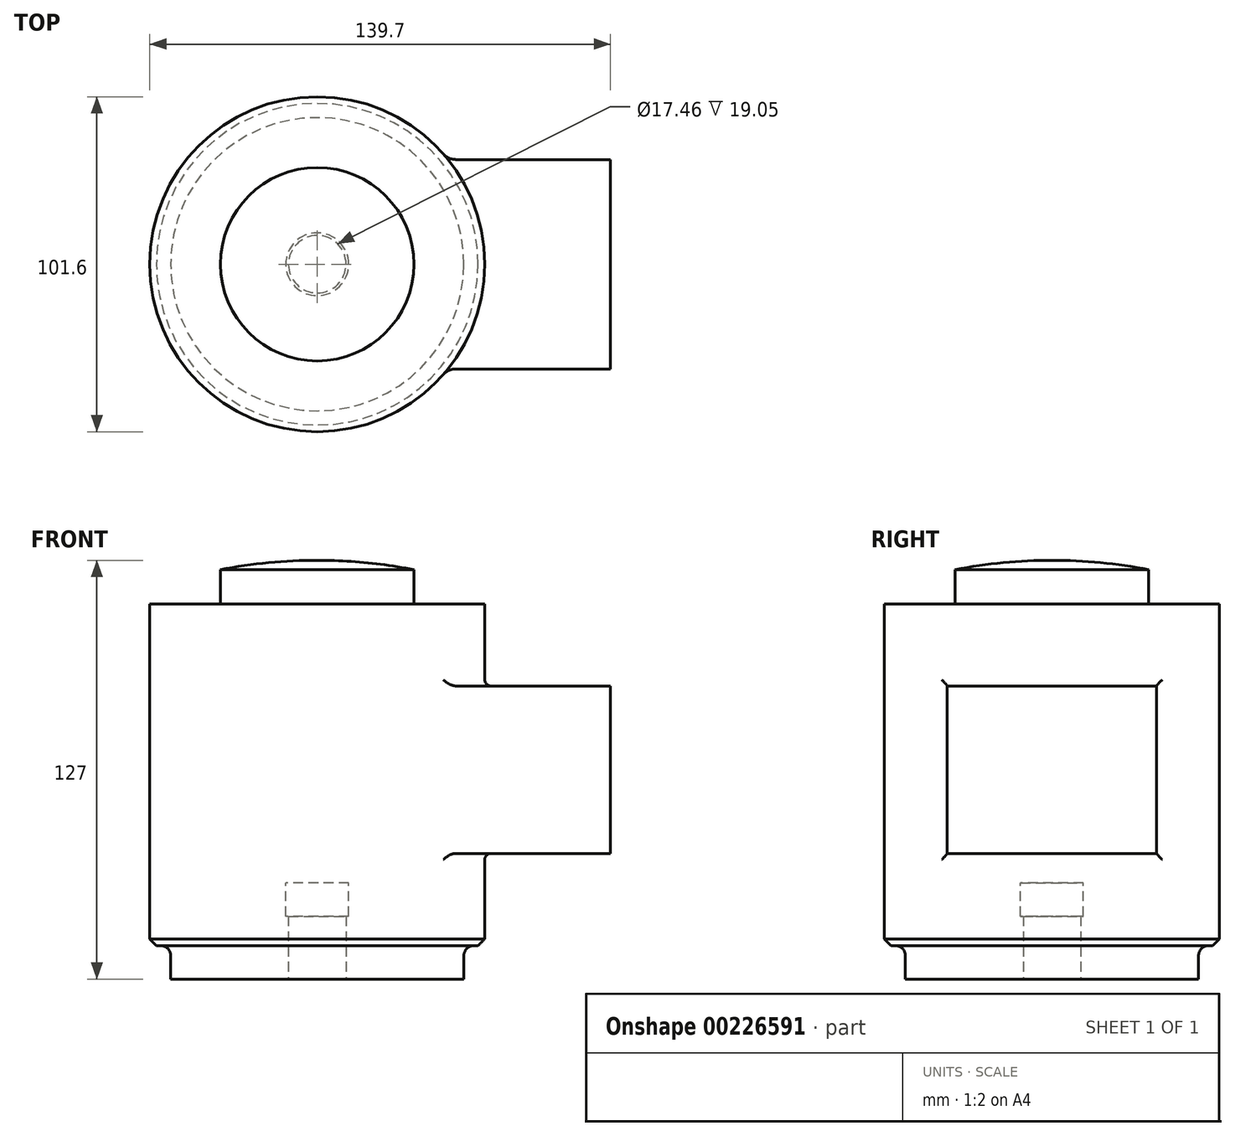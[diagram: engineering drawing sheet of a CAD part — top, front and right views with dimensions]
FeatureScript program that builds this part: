
annotation { "Feature Type Name" : "Feature", "Feature Type Description" : "" }
export const myFeature = defineFeature(function(context is Context, id is Id, definition is map)
    precondition{}
    {
        {
            var Q0;
            Q0=qCreatedBy(makeId("Front.planeOp"),FACE);
            var sketch = newSketch(context, id + "F0", { "sketchPlane" : qUnion([Q0])});
            skLineSegment(sketch, "E0.bottom", {"start": v(44.45, 0) * mm, "end": v(-44.45, 0) * mm});
            skLineSegment(sketch, "E0.top", {"start": v(44.45, 10.16) * mm, "end": v(-44.45, 10.16) * mm});
            skLineSegment(sketch, "E0.left", {"start": v(44.45, 0) * mm, "end": v(44.45, 10.16) * mm});
            skLineSegment(sketch, "E0.right", {"start": v(-44.45, 0) * mm, "end": v(-44.45, 10.16) * mm});
            skLineSegment(sketch, "E1.bottom", {"start": v(50.8, 10.16) * mm, "end": v(-50.8, 10.16) * mm});
            skLineSegment(sketch, "E1.top", {"start": v(50.8, 113.8) * mm, "end": v(-50.8, 113.8) * mm});
            skLineSegment(sketch, "E1.left", {"start": v(50.8, 10.16) * mm, "end": v(50.8, 113.8) * mm});
            skLineSegment(sketch, "E1.right", {"start": v(-50.8, 10.16) * mm, "end": v(-50.8, 113.8) * mm});
            skPoint(sketch, "E1.middle", {"position": v(0, 61.98) * mm});
            skLineSegment(sketch, "E2.bottom", {"start": v(29.34, 113.8) * mm, "end": v(-29.34, 113.8) * mm});
            skLineSegment(sketch, "E2.top", {"start": v(29.34, 124.15) * mm, "end": v(-29.34, 124.15) * mm});
            skLineSegment(sketch, "E2.left", {"start": v(29.34, 113.8) * mm, "end": v(29.34, 124.15) * mm});
            skLineSegment(sketch, "E2.right", {"start": v(-29.34, 113.8) * mm, "end": v(-29.34, 124.15) * mm});
            skPoint(sketch, "E2.middle", {"position": v(0, 118.97) * mm});
            skArc(sketch, "E3", {"start": v(29.34, 124.15) * mm, "mid": v(0, 127) * mm, "end": v(-29.34, 124.15) * mm});
            skLineSegment(sketch, "E4.bottom", {"start": v(0, 38.1) * mm, "end": v(88.9, 38.1) * mm});
            skLineSegment(sketch, "E4.top", {"start": v(0, 88.9) * mm, "end": v(88.9, 88.9) * mm});
            skLineSegment(sketch, "E4.left", {"start": v(0, 38.1) * mm, "end": v(0, 88.9) * mm});
            skLineSegment(sketch, "E4.right", {"start": v(88.9, 38.1) * mm, "end": v(88.9, 88.9) * mm});
            skLineSegment(sketch, "E5", {"start": v(0, 0) * mm, "end": v(0, 127) * mm});
            skLineSegment(sketch, "E6.bottom", {"start": v(9.53, 19.05) * mm, "end": v(-9.52, 19.05) * mm});
            skLineSegment(sketch, "E6.top", {"start": v(9.53, 29.21) * mm, "end": v(-9.52, 29.21) * mm});
            skLineSegment(sketch, "E6.left", {"start": v(9.53, 19.05) * mm, "end": v(9.53, 29.21) * mm});
            skLineSegment(sketch, "E6.right", {"start": v(-9.53, 19.05) * mm, "end": v(-9.52, 29.21) * mm});
            skPoint(sketch, "E6.middle", {"position": v(0, 24.13) * mm});
            skSolve(sketch);
        }
        {
            var Q0;
            {var subQ0=sQuery(id+"F0.wireOp",EDGE,"E0.right");Q0=makeQuery(id+"F0.imprint","IMPRINT",FACE,{"disambiguationData":[TD([[makeQuery(id+"F0.imprint","IMPRINT",EDGE,{"derivedFrom":subQ0}),-1.0]])]});}
            var Q1;
            {var subQ0=sQuery(id+"F0.wireOp",EDGE,"E1.right");Q1=makeQuery(id+"F0.imprint","IMPRINT",FACE,{"disambiguationData":[TD([[makeQuery(id+"F0.imprint","IMPRINT",EDGE,{"derivedFrom":subQ0}),-1.0]])]});}
            var Q2;
            {var subQ5=sQuery(id+"F0.wireOp",EDGE,"8SzRcd8H-i3ES-h9Rq-7Vuq-7DKlFg5wnlTV.right");Q2=makeQuery(id+"F0.imprint","IMPRINT",FACE,{"disambiguationData":[TD([[makeQuery(id+"F0.imprint","IMPRINT",EDGE,{"derivedFrom":subQ5}),-1.0]])]});}
            var Q3;
            {var subQ0=sQuery(id+"F0.wireOp",EDGE,"E2.right");Q3=makeQuery(id+"F0.imprint","IMPRINT",FACE,{"disambiguationData":[TD([[makeQuery(id+"F0.imprint","IMPRINT",EDGE,{"derivedFrom":subQ0}),-1.0]])]});}
            var Q4;
            {var subQ0=sQuery(id+"F0.wireOp",EDGE,"E3");var subQ3=sQuery(id+"F0.wireOp",EDGE,"E5");var subQ5=makeQuery(id+"F0.imprint","INTERSECT",VERTEX,{"derivedFrom":[subQ0,subQ3]});Q4=makeQuery(id+"F0.imprint","IMPRINT",FACE,{"disambiguationData":[TD([[makeQuery(id+"F0.imprint","IMPRINT",EDGE,{"disambiguationData":[TD([[subQ5,1.0]])],"derivedFrom":subQ3}),1.0]])]});}
            var Q5;
            Q5=sQuery(id+"F0.wireOp",EDGE,"E4.left");
            revolve(context, id + "F1", {"entities" : qUnion([Q0, Q1, Q2, Q3, Q4]), "axis" : qUnion([Q5]), "revolveType" : RevolveType.FULL, "oppositeDirection" : true});
        }
        {
            var Q0;
            {var subQ5=sQuery(id+"F0.wireOp",EDGE,"E4.right");Q0=makeQuery(id+"F0.imprint","IMPRINT",FACE,{"disambiguationData":[TD([[makeQuery(id+"F0.imprint","IMPRINT",EDGE,{"derivedFrom":subQ5}),1.0]])]});}
            var Q1;
            {var subQ0=sQuery(id+"F0.wireOp",EDGE,"E4.bottom");var subQ1=sQuery(id+"F0.wireOp",EDGE,"E1.left");var subQ2=makeQuery(id+"F0.imprint","INTERSECT",VERTEX,{"derivedFrom":[subQ1,subQ0]});Q1=makeQuery(id+"F0.imprint","IMPRINT",FACE,{"disambiguationData":[TD([[makeQuery(id+"F0.imprint","IMPRINT",EDGE,{"disambiguationData":[TD([[subQ2,-1.0]])],"derivedFrom":subQ1}),1.0]])]});}
            extrude(context, id + "F2", {"entities" : qUnion([Q0, Q1]), "operationType" : NewBodyOperationType.ADD, "depth" : 63.5 * mm, "symmetric" : true});
        }
        {
            var Q0;
            Q0=makeQuery(id+"F1.opRevolve","SWEPT_EDGE",EDGE,{"disambiguationData":[OSD([sQuery(id+"F0.wireOp",EDGE,"E1.bottom"),sQuery(id+"F0.wireOp",EDGE,"E1.right")])]});
            chamfer(context, id + "F3", {"entities" : qUnion([Q0]), "width" : 2.03 * mm, "tangentPropagation" : true});
        }
        {
            var Q0;
            Q0=makeQuery(id+"F1.opRevolve","SWEPT_EDGE",EDGE,{"disambiguationData":[OSD([sQuery(id+"F0.wireOp",EDGE,"E0.right"),sQuery(id+"F0.wireOp",EDGE,"E1.bottom")])]});
            fillet(context, id + "F4", {"entities" : qUnion([Q0]), "radius" : 3.05 * mm, "tangentPropagation" : true, "allowEdgeOverflow" : false});
        }
        {
            var Q0;
            Q0=qCreatedBy(makeId("Top.planeOp"),FACE);
            var sketch = newSketch(context, id + "F5", { "sketchPlane" : qUnion([Q0])});
            skCircle(sketch, "E7", {"center": v(0, 0) * mm, "radius": 26.37 * mm});
            skSolve(sketch);
        }
        {
            var Q0;
            Q0=sQuery(id+"F5.wireOp",VERTEX,"E7.center");
            var Q1;
            Q1=makeQuery(id+"F1.opRevolve","SWEPT_BODY",BODY,{"disambiguationData":[OSD([sQuery(id+"F0.wireOp",EDGE,"E0.bottom"),sQuery(id+"F0.wireOp",EDGE,"E0.right"),sQuery(id+"F0.wireOp",EDGE,"E1.bottom"),sQuery(id+"F0.wireOp",EDGE,"E1.top"),sQuery(id+"F0.wireOp",EDGE,"E1.right"),sQuery(id+"F0.wireOp",EDGE,"E2.right"),sQuery(id+"F0.wireOp",EDGE,"E3"),sQuery(id+"F0.wireOp",EDGE,"E5")])]});
            hole(context, id + "F6", {"style" : HoleStyle.SIMPLE, "endStyle" : HoleEndStyle.BLIND, "oppositeDirection" : true, "standardTappedOrClearance" : lookupTablePath({ "standard" : "ANSI", "engagement" : "75%", "pitch" : "16 tpi", "size" : "3/4", "type" : "Tapped" }), "standardBlindInLast" : lookupTablePath({ "standard" : "ANSI", "engagement" : "75%", "pitch" : "16 tpi", "size" : "3/4", "type" : "Tapped" }), "holeDiameter" : 17.46 * mm, "holeDepth" : 19.05 * mm, "locations" : qUnion([Q0]), "scope" : qUnion([Q1]), "majorDiameter" : 19.05 * mm});
        }
        {
            var Q0;
            {var subQ5=sQuery(id+"F0.wireOp",EDGE,"E6.right");Q0=makeQuery(id+"F0.imprint","IMPRINT",FACE,{"disambiguationData":[TD([[makeQuery(id+"F0.imprint","IMPRINT",EDGE,{"derivedFrom":subQ5}),-1.0]])]});}
            var Q1;
            Q1=sQuery(id+"F0.wireOp",EDGE,"E5");
            revolve(context, id + "F7", {"operationType" : NewBodyOperationType.REMOVE, "entities" : qUnion([Q0]), "axis" : qUnion([Q1]), "revolveType" : RevolveType.FULL, "oppositeDirection" : true});
        }
        {
            var Q0;
            Q0=makeQuery(id+"F2.boolean.opBoolean","INTERSECT",EDGE,{"derivedFrom":[makeQuery(id+"F1.opRevolve","SWEPT_FACE",FACE,{"disambiguationData":[OSD([sQuery(id+"F0.wireOp",EDGE,"E1.right")])]}),makeQuery(id+"F2.opExtrude","CAP_FACE",FACE,{"disambiguationData":[OSD([sQuery(id+"F0.wireOp",EDGE,"E4.bottom"),sQuery(id+"F0.wireOp",EDGE,"E4.top"),sQuery(id+"F0.wireOp",EDGE,"E4.right"),sQuery(id+"F0.wireOp",EDGE,"E5")])],"isStart":false})]});
            var Q1;
            Q1=makeQuery(id+"F2.boolean.opBoolean","INTERSECT",EDGE,{"derivedFrom":[makeQuery(id+"F1.opRevolve","SWEPT_FACE",FACE,{"disambiguationData":[OSD([sQuery(id+"F0.wireOp",EDGE,"E1.right")])]}),makeQuery(id+"F2.opExtrude","CAP_FACE",FACE,{"disambiguationData":[OSD([sQuery(id+"F0.wireOp",EDGE,"E4.bottom"),sQuery(id+"F0.wireOp",EDGE,"E4.top"),sQuery(id+"F0.wireOp",EDGE,"E4.right"),sQuery(id+"F0.wireOp",EDGE,"E5")])],"isStart":true})]});
            fillet(context, id + "F8", {"entities" : qUnion([Q0, Q1]), "radius" : 5.08 * mm, "tangentPropagation" : true, "allowEdgeOverflow" : false});
        }
        {
            var Q0;
            Q0=makeQuery(id+"F2.boolean.opBoolean","INTERSECT",EDGE,{"derivedFrom":[makeQuery(id+"F1.opRevolve","SWEPT_FACE",FACE,{"disambiguationData":[OSD([sQuery(id+"F0.wireOp",EDGE,"E1.right")])]}),makeQuery(id+"F2.opExtrude","SWEPT_FACE",FACE,{"disambiguationData":[OSD([sQuery(id+"F0.wireOp",EDGE,"E4.top")])]})]});
            var Q1;
            Q1=makeQuery(id+"F2.boolean.opBoolean","INTERSECT",EDGE,{"derivedFrom":[makeQuery(id+"F1.opRevolve","SWEPT_FACE",FACE,{"disambiguationData":[OSD([sQuery(id+"F0.wireOp",EDGE,"E1.right")])]}),makeQuery(id+"F2.opExtrude","SWEPT_FACE",FACE,{"disambiguationData":[OSD([sQuery(id+"F0.wireOp",EDGE,"E4.bottom")])]})]});
            fillet(context, id + "F9", {"entities" : qUnion([Q0, Q1]), "radius" : 1.88 * mm, "tangentPropagation" : true, "allowEdgeOverflow" : false});
        }
    });
